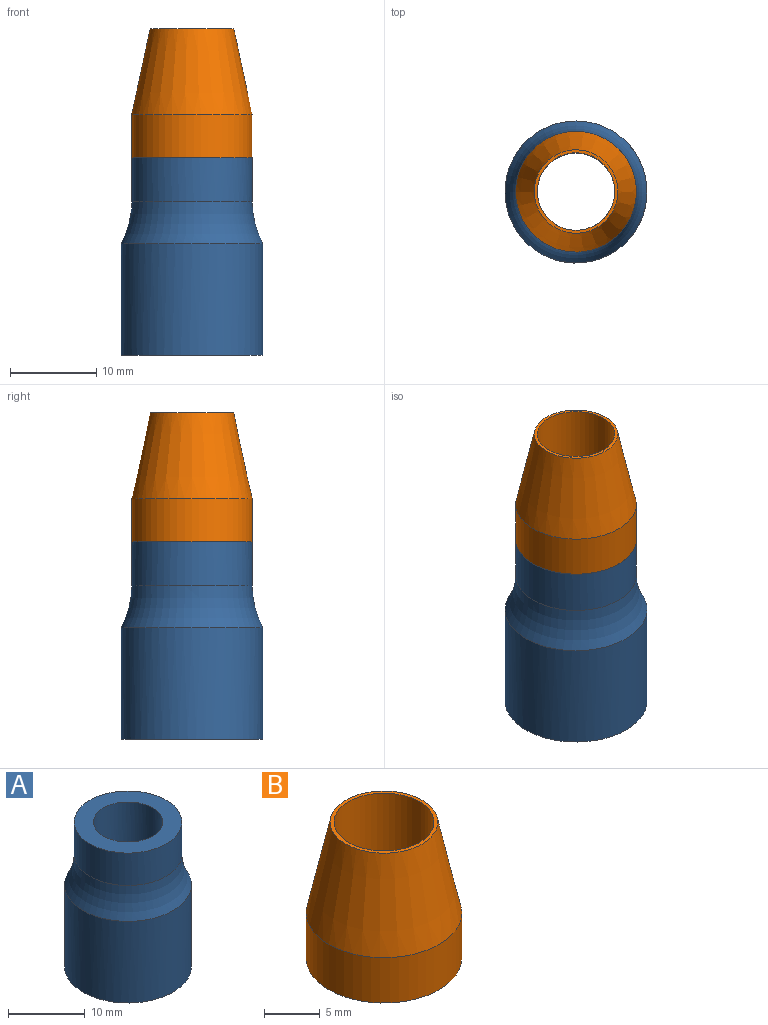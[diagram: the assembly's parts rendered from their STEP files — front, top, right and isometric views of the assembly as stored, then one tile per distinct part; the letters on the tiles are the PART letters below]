
ASSEMBLY  parts=2 mates=1
PART A: 8 faces, bbox 21.4x21.4x24.9 mm
  f0: cylinder r=5.5mm len=11mm, axis (0,0,-1), area 345.6mm2, adj f2,f7
  f1: cylinder r=8.25mm len=16.5mm, axis (0,0,-1), area 673.9mm2, adj f2,f6
  f2: plane 16.5x16.5mm, normal (0,0,-1), area 118.8mm2, adj f0,f1
  f3: cylinder r=4.5mm len=9.13mm, axis (0,0,-1), area 258.1mm2, adj f5,f7
  f4: cylinder r=7mm len=14mm, axis (0,0,-1), area 226.9mm2, adj f5,f6
  f5: plane 14x14mm, normal (0,0,1), area 90.3mm2, adj f3,f4
  f6: torus R=17mm, axis (0,0,-1), area 235.6mm2, adj f1,f4
  f7: torus R=12.5mm, axis (0,0,-1), area 122.8mm2, adj f0,f3
PART B: 5 faces, bbox 14x14x15 mm
  f0: plane 9.7x9.7mm, normal (0,0,1), area 10.3mm2, adj f1,f4
  f1: cone r=4.85mm half-angle=12.1deg, axis (0,0,-1), area 380.8mm2, adj f0,f2
  f2: cylinder r=7mm len=14mm, axis (0,0,1), area 219.9mm2, adj f1,f3
  f3: plane 14x14mm, normal (0,0,-1), area 90.3mm2, adj f2,f4
  f4: cylinder r=4.5mm len=15mm, axis (0,0,-1), area 424.1mm2, adj f0,f3
PLACE A t=(10.83,13.44,0.94)mm
PLACE B t=(10.83,13.44,28.94)mm
MATE fastened A.f0 <-> B.f1  axis (0,0,1) through (10.83,13.44,23.94)mm
